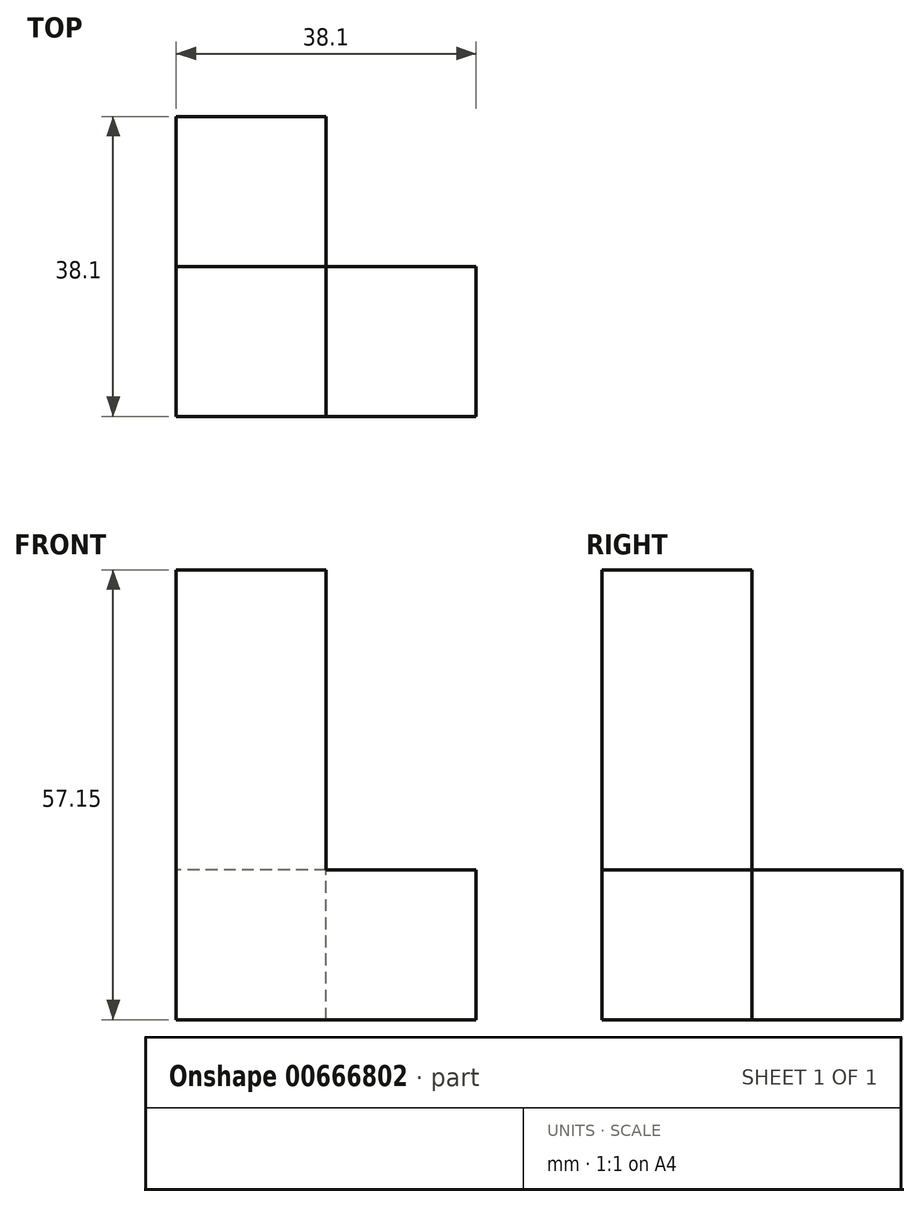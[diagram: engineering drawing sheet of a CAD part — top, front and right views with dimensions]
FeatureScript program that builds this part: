
annotation { "Feature Type Name" : "Feature", "Feature Type Description" : "" }
export const myFeature = defineFeature(function(context is Context, id is Id, definition is map)
    precondition{}
    {
        {
            var Q0;
            Q0=qCreatedBy(makeId("Front.planeOp"),FACE);
            var sketch = newSketch(context, id + "F0", { "sketchPlane" : qUnion([Q0])});
            skLineSegment(sketch, "E0", {"start": v(0, 0) * mm, "end": v(38.1, 0) * mm});
            skLineSegment(sketch, "E1", {"start": v(38.1, 0) * mm, "end": v(38.1, 19.05) * mm});
            skLineSegment(sketch, "E2", {"start": v(38.1, 19.05) * mm, "end": v(19.05, 19.05) * mm});
            skLineSegment(sketch, "E3", {"start": v(19.05, 19.05) * mm, "end": v(19.05, 57.15) * mm});
            skLineSegment(sketch, "E4", {"start": v(19.05, 57.15) * mm, "end": v(0, 57.15) * mm});
            skLineSegment(sketch, "E5", {"start": v(0, 57.15) * mm, "end": v(0, 0) * mm});
            skSolve(sketch);
        }
        {
            var Q0;
            Q0=makeQuery(id+"F0.imprint","IMPRINT",FACE,{"disambiguationData":[TD([[makeQuery(id+"F0.imprint","IMPRINT",EDGE,{"derivedFrom":sQuery(id+"F0.wireOp",EDGE,"E0")}),1.0]])]});
            extrude(context, id + "F1", {"entities" : qUnion([Q0]), "depth" : 38.1 * mm, "offsetDistance" : 25.4 * mm});
        }
        {
            var Q0;
            Q0=makeQuery(id+"F1.opExtrude","SWEPT_FACE",FACE,{"disambiguationData":[OSD([sQuery(id+"F0.wireOp",EDGE,"E3")])]});
            var sketch = newSketch(context, id + "F2", { "sketchPlane" : qUnion([Q0])});
            skLineSegment(sketch, "E6.bottom", {"start": v(0, 57.15) * mm, "end": v(-19.05, 57.15) * mm});
            skLineSegment(sketch, "E6.top", {"start": v(0, 19.05) * mm, "end": v(-19.05, 19.05) * mm});
            skLineSegment(sketch, "E6.left", {"start": v(0, 57.15) * mm, "end": v(0, 19.05) * mm});
            skLineSegment(sketch, "E6.right", {"start": v(-19.05, 57.15) * mm, "end": v(-19.05, 19.05) * mm});
            skSolve(sketch);
        }
        {
            var Q0;
            Q0=makeQuery(id+"F2.imprint","IMPRINT",FACE,{"disambiguationData":[TD([[makeQuery(id+"F2.imprint","IMPRINT",EDGE,{"derivedFrom":sQuery(id+"F2.wireOp",EDGE,"E6.bottom")}),-1.0]])]});
            extrude(context, id + "F3", {"entities" : qUnion([Q0]), "operationType" : NewBodyOperationType.REMOVE, "oppositeDirection" : true, "depth" : 25.4 * mm, "offsetDistance" : 25.4 * mm});
        }
        {
            var Q0;
            Q0=makeQuery(id+"F3.boolean.opBoolean","MERGE",FACE,{"derivedFrom":[makeQuery(id+"F1.opExtrude","SWEPT_FACE",FACE,{"disambiguationData":[OSD([sQuery(id+"F0.wireOp",EDGE,"E2")])]}),makeQuery(id+"F3.opExtrude","SWEPT_FACE",FACE,{"disambiguationData":[OSD([sQuery(id+"F2.wireOp",EDGE,"E6.top")])]})]});
            var sketch = newSketch(context, id + "F4", { "sketchPlane" : qUnion([Q0])});
            skLineSegment(sketch, "E7.bottom", {"start": v(38.1, 0) * mm, "end": v(19.05, 0) * mm});
            skLineSegment(sketch, "E7.top", {"start": v(38.1, -19.05) * mm, "end": v(19.05, -19.05) * mm});
            skLineSegment(sketch, "E7.left", {"start": v(38.1, 0) * mm, "end": v(38.1, -19.05) * mm});
            skLineSegment(sketch, "E7.right", {"start": v(19.05, 0) * mm, "end": v(19.05, -19.05) * mm});
            skSolve(sketch);
        }
        {
            var Q0;
            Q0=makeQuery(id+"F4.imprint","IMPRINT",FACE,{"disambiguationData":[TD([[makeQuery(id+"F4.imprint","IMPRINT",EDGE,{"derivedFrom":sQuery(id+"F4.wireOp",EDGE,"E7.bottom")}),1.0]])]});
            extrude(context, id + "F5", {"entities" : qUnion([Q0]), "operationType" : NewBodyOperationType.REMOVE, "oppositeDirection" : true, "depth" : 25.4 * mm, "offsetDistance" : 25.4 * mm});
        }
    });
